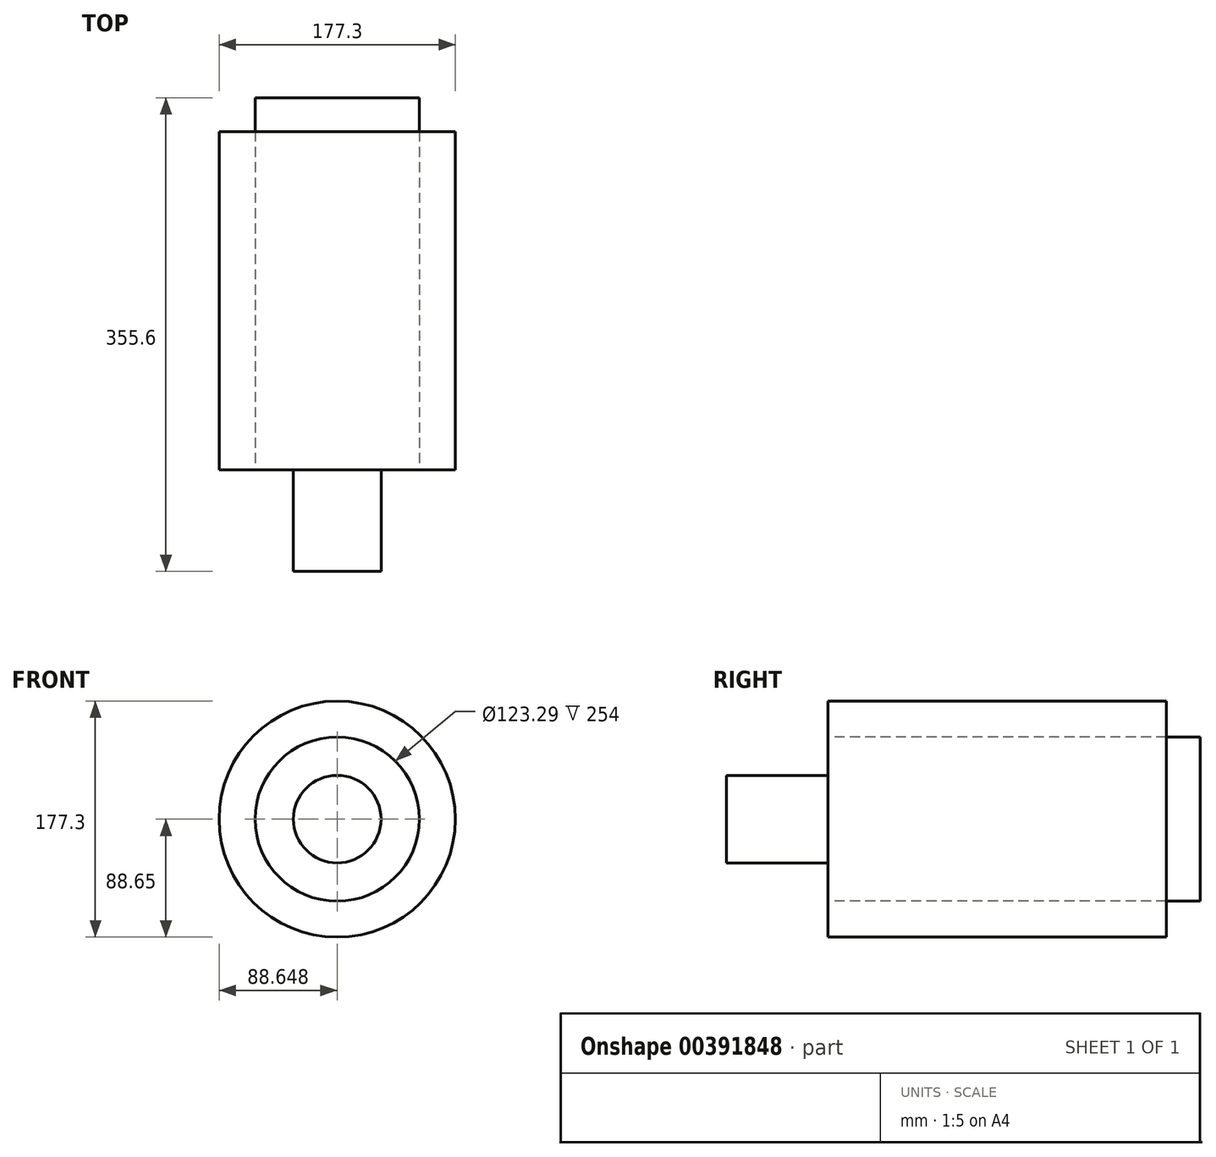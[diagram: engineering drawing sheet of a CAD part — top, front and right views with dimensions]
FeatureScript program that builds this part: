
annotation { "Feature Type Name" : "Feature", "Feature Type Description" : "" }
export const myFeature = defineFeature(function(context is Context, id is Id, definition is map)
    precondition{}
    {
        {
            var Q0;
            Q0=qCreatedBy(makeId("Front.planeOp"),FACE);
            var sketch = newSketch(context, id + "F0", { "sketchPlane" : qUnion([Q0])});
            skCircle(sketch, "E0", {"center": v(-21.85, 0) * mm, "radius": 32.9 * mm});
            skCircle(sketch, "E1", {"center": v(-21.85, 0) * mm, "radius": 61.64 * mm});
            skCircle(sketch, "E2", {"center": v(-21.85, 0) * mm, "radius": 88.65 * mm});
            skSolve(sketch);
        }
        {
            var Q0;
            Q0=makeQuery(id+"F0.imprint","IMPRINT",FACE,{"disambiguationData":[TD([[makeQuery(id+"F0.imprint","IMPRINT",EDGE,{"derivedFrom":sQuery(id+"F0.wireOp",EDGE,"E0")}),1.0]])]});
            extrude(context, id + "F1", {"entities" : qUnion([Q0]), "depth" : 76.2 * mm, "hasSecondDirection" : true, "secondDirectionOppositeDirection" : true, "secondDirectionDepth" : 279.4 * mm});
        }
        {
            var Q0;
            Q0=makeQuery(id+"F0.imprint","IMPRINT",FACE,{"disambiguationData":[TD([[makeQuery(id+"F0.imprint","IMPRINT",EDGE,{"derivedFrom":sQuery(id+"F0.wireOp",EDGE,"E0")}),-1.0]])]});
            extrude(context, id + "F2", {"entities" : qUnion([Q0]), "operationType" : NewBodyOperationType.ADD, "oppositeDirection" : true, "depth" : 279.4 * mm});
        }
        {
            var Q0;
            Q0=makeQuery(id+"F0.imprint","IMPRINT",FACE,{"disambiguationData":[TD([[makeQuery(id+"F0.imprint","IMPRINT",EDGE,{"derivedFrom":sQuery(id+"F0.wireOp",EDGE,"E1")}),-1.0]])]});
            extrude(context, id + "F3", {"entities" : qUnion([Q0]), "oppositeDirection" : true, "depth" : 254 * mm});
        }
    });
